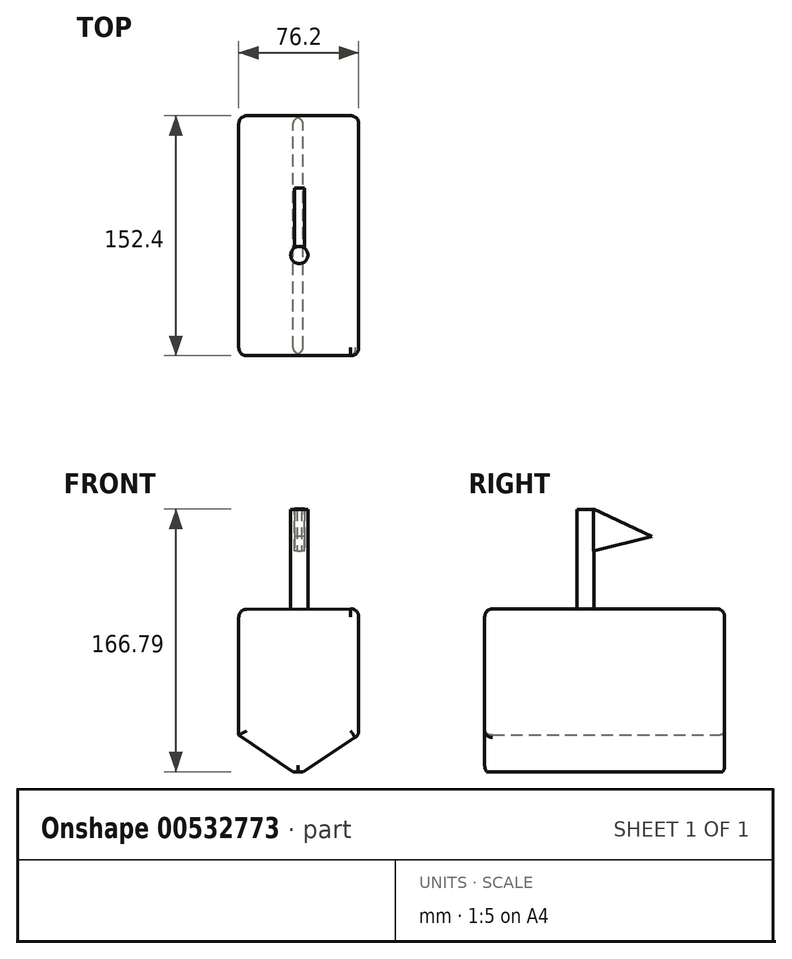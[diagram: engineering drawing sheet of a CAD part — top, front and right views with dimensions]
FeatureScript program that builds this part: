
annotation { "Feature Type Name" : "Feature", "Feature Type Description" : "" }
export const myFeature = defineFeature(function(context is Context, id is Id, definition is map)
    precondition{}
    {
        {
            var Q0;
            Q0=qCreatedBy(makeId("Front.planeOp"),FACE);
            var sketch = newSketch(context, id + "F0", { "sketchPlane" : qUnion([Q0])});
            skLineSegment(sketch, "E0", {"start": v(-58.77, 49.84) * mm, "end": v(-58.77, -30.07) * mm});
            skLineSegment(sketch, "E1", {"start": v(-58.77, -30.07) * mm, "end": v(-24.38, -53.34) * mm});
            skLineSegment(sketch, "E2", {"start": v(-24.38, -53.34) * mm, "end": v(-17.97, -53.34) * mm});
            skLineSegment(sketch, "E3", {"start": v(-17.97, -53.34) * mm, "end": v(17.43, -30.07) * mm});
            skLineSegment(sketch, "E4", {"start": v(17.43, -30.07) * mm, "end": v(17.43, 50.17) * mm});
            skLineSegment(sketch, "E5", {"start": v(-58.77, 49.84) * mm, "end": v(17.43, 50.17) * mm});
            skSolve(sketch);
        }
        {
            var Q0;
            Q0=makeQuery(id+"F0.imprint","IMPRINT",FACE,{"disambiguationData":[TD([[makeQuery(id+"F0.imprint","IMPRINT",EDGE,{"derivedFrom":sQuery(id+"F0.wireOp",EDGE,"E0")}),1.0]])]});
            extrude(context, id + "F1", {"entities" : qUnion([Q0]), "depth" : 152.4 * mm, "offsetDistance" : 25.4 * mm});
        }
        {
            var Q0;
            Q0=makeQuery(id+"F1.opExtrude","SWEPT_EDGE",EDGE,{"disambiguationData":[OSD([sQuery(id+"F0.wireOp",EDGE,"E0"),sQuery(id+"F0.wireOp",EDGE,"E5")])]});
            var Q1;
            Q1=makeQuery(id+"F1.opExtrude","CAP_EDGE",EDGE,{"disambiguationData":[OSD([sQuery(id+"F0.wireOp",EDGE,"E0")])],"isStart":false});
            var Q2;
            Q2=makeQuery(id+"F1.opExtrude","CAP_EDGE",EDGE,{"disambiguationData":[OSD([sQuery(id+"F0.wireOp",EDGE,"E4")])],"isStart":false});
            var Q3;
            Q3=makeQuery(id+"F1.opExtrude","CAP_EDGE",EDGE,{"disambiguationData":[OSD([sQuery(id+"F0.wireOp",EDGE,"E5")])],"isStart":false});
            var Q4;
            Q4=makeQuery(id+"F1.opExtrude","CAP_EDGE",EDGE,{"disambiguationData":[OSD([sQuery(id+"F0.wireOp",EDGE,"E1")])],"isStart":false});
            var Q5;
            Q5=makeQuery(id+"F1.opExtrude","CAP_EDGE",EDGE,{"disambiguationData":[OSD([sQuery(id+"F0.wireOp",EDGE,"E3")])],"isStart":false});
            fillet(context, id + "F2", {"entities" : qUnion([Q0, Q1, Q2, Q3, Q4, Q5]), "radius" : 5.08 * mm, "tangentPropagation" : true, "allowEdgeOverflow" : false});
        }
        {
            var Q0;
            Q0=qCreatedBy(makeId("Right.planeOp"),FACE);
            cPlane(context, id + "F3", {"entities" : qUnion([Q0]), "cplaneType" : CPlaneType.OFFSET, "offset" : 20.32 * mm, "oppositeDirection" : true, "width" : 152.4 * mm, "height" : 152.4 * mm});
        }
        {
            var Q0;
            Q0=qCreatedBy(id+"F3.planeOp",FACE);
            var sketch = newSketch(context, id + "F4", { "sketchPlane" : qUnion([Q0])});
            skLineSegment(sketch, "E6.bottom", {"start": v(-82.97, 113.36) * mm, "end": v(-93.9, 113.36) * mm});
            skLineSegment(sketch, "E6.top", {"start": v(-82.97, 49.86) * mm, "end": v(-93.9, 49.86) * mm});
            skLineSegment(sketch, "E6.left", {"start": v(-82.97, 113.36) * mm, "end": v(-82.97, 49.86) * mm});
            skLineSegment(sketch, "E6.right", {"start": v(-93.9, 113.36) * mm, "end": v(-93.9, 49.86) * mm});
            skLineSegment(sketch, "E7", {"start": v(-88.44, 49.86) * mm, "end": v(-88.44, 126.97) * mm});
            skSolve(sketch);
        }
        {
            var Q0;
            {var subQ0=sQuery(id+"F4.wireOp",EDGE,"E6.left");Q0=makeQuery(id+"F4.imprint","IMPRINT",FACE,{"disambiguationData":[TD([[makeQuery(id+"F4.imprint","IMPRINT",EDGE,{"derivedFrom":subQ0}),-1.0]])]});}
            var Q1;
            Q1=sQuery(id+"F4.wireOp",EDGE,"E7");
            revolve(context, id + "F5", {"operationType" : NewBodyOperationType.ADD, "entities" : qUnion([Q0]), "axis" : qUnion([Q1]), "revolveType" : RevolveType.FULL});
        }
        {
            var Q0;
            Q0=qCreatedBy(id+"F3.planeOp",FACE);
            var sketch = newSketch(context, id + "F6", { "sketchPlane" : qUnion([Q0])});
            skLineSegment(sketch, "E8", {"start": v(-83.2, 113.45) * mm, "end": v(-46.04, 96.25) * mm});
            skLineSegment(sketch, "E9", {"start": v(-46.04, 96.25) * mm, "end": v(-83.2, 86.96) * mm});
            skLineSegment(sketch, "E10", {"start": v(-83.2, 86.96) * mm, "end": v(-83.2, 113.45) * mm});
            skSolve(sketch);
        }
        {
            var Q0;
            Q0=makeQuery(id+"F6.imprint","IMPRINT",FACE,{"disambiguationData":[TD([[makeQuery(id+"F6.imprint","IMPRINT",EDGE,{"derivedFrom":sQuery(id+"F6.wireOp",EDGE,"E8")}),-1.0]])]});
            extrude(context, id + "F7", {"entities" : qUnion([Q0]), "operationType" : NewBodyOperationType.ADD, "endBound" : BoundingType.SYMMETRIC, "depth" : 6.35 * mm, "offsetDistance" : 25.4 * mm});
        }
        {
            var Q0;
            Q0=makeQuery(id+"F1.opExtrude","SWEPT_EDGE",EDGE,{"disambiguationData":[OSD([sQuery(id+"F0.wireOp",EDGE,"E4"),sQuery(id+"F0.wireOp",EDGE,"E5")])]});
            var Q1;
            Q1=makeQuery(id+"F1.opExtrude","SWEPT_EDGE",EDGE,{"disambiguationData":[OSD([sQuery(id+"F0.wireOp",EDGE,"E3"),sQuery(id+"F0.wireOp",EDGE,"E4")])]});
            var Q2;
            Q2=makeQuery(id+"F1.opExtrude","CAP_EDGE",EDGE,{"disambiguationData":[OSD([sQuery(id+"F0.wireOp",EDGE,"E0")])],"isStart":true});
            var Q3;
            Q3=makeQuery(id+"F1.opExtrude","CAP_EDGE",EDGE,{"disambiguationData":[OSD([sQuery(id+"F0.wireOp",EDGE,"E1")])],"isStart":true});
            var Q4;
            Q4=makeQuery(id+"F1.opExtrude","CAP_EDGE",EDGE,{"disambiguationData":[OSD([sQuery(id+"F0.wireOp",EDGE,"E3")])],"isStart":true});
            var Q5;
            Q5=makeQuery(id+"F1.opExtrude","CAP_EDGE",EDGE,{"disambiguationData":[OSD([sQuery(id+"F0.wireOp",EDGE,"E4")])],"isStart":true});
            fillet(context, id + "F8", {"entities" : qUnion([Q0, Q1, Q2, Q3, Q4, Q5]), "radius" : 5.08 * mm, "tangentPropagation" : true, "allowEdgeOverflow" : false});
        }
    });
